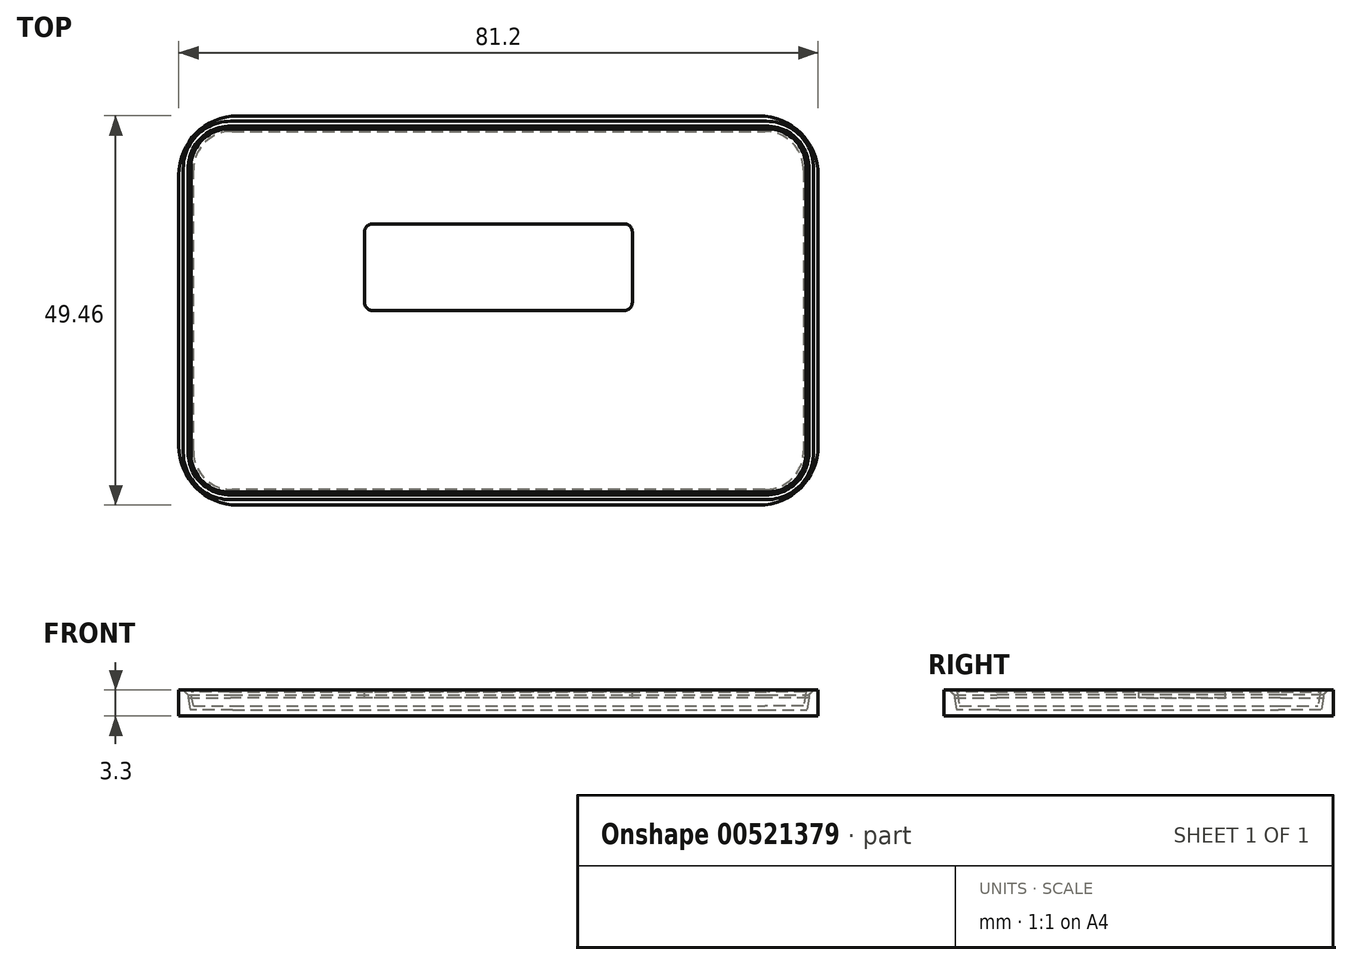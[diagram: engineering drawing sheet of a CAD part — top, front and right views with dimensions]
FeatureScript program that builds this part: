
annotation { "Feature Type Name" : "Feature", "Feature Type Description" : "" }
export const myFeature = defineFeature(function(context is Context, id is Id, definition is map)
    precondition{}
    {
        {
            var Q0;
            Q0=qCreatedBy(makeId("Top.planeOp"),FACE);
            var sketch = newSketch(context, id + "F0", { "sketchPlane" : qUnion([Q0])});
            skLineSegment(sketch, "E0.bottom", {"start": v(-38.75, 22.75) * mm, "end": v(38.75, 22.75) * mm});
            skLineSegment(sketch, "E0.top", {"start": v(-38.75, -22.75) * mm, "end": v(38.75, -22.75) * mm});
            skLineSegment(sketch, "E0.left", {"start": v(-38.75, 22.75) * mm, "end": v(-38.75, -22.75) * mm});
            skLineSegment(sketch, "E0.right", {"start": v(38.75, 22.75) * mm, "end": v(38.75, -22.75) * mm});
            skPoint(sketch, "E0.middle", {"position": v(0, 0) * mm});
            skSolve(sketch);
        }
        {
            var Q0;
            Q0 = qSketchRegion(id + "F0", true);
            extrude(context, id + "F1", {"entities" : qUnion([Q0]), "depth" : 1.8 * mm, "offsetDistance" : 25 * mm, "hasDraft" : true, "draftAngle" : 10 * degree});
        }
        {
            var Q0;
            Q0=makeQuery(id+"F1.opExtrude","SWEPT_EDGE",EDGE,{"disambiguationData":[OSD([sQuery(id+"F0.wireOp",EDGE,"E0.bottom"),sQuery(id+"F0.wireOp",EDGE,"E0.left")])]});
            var Q1;
            Q1=makeQuery(id+"F1.opExtrude","SWEPT_EDGE",EDGE,{"disambiguationData":[OSD([sQuery(id+"F0.wireOp",EDGE,"E0.top"),sQuery(id+"F0.wireOp",EDGE,"E0.left")])]});
            var Q2;
            Q2=makeQuery(id+"F1.opExtrude","SWEPT_EDGE",EDGE,{"disambiguationData":[OSD([sQuery(id+"F0.wireOp",EDGE,"E0.top"),sQuery(id+"F0.wireOp",EDGE,"E0.right")])]});
            var Q3;
            Q3=makeQuery(id+"F1.opExtrude","SWEPT_EDGE",EDGE,{"disambiguationData":[OSD([sQuery(id+"F0.wireOp",EDGE,"E0.bottom"),sQuery(id+"F0.wireOp",EDGE,"E0.right")])]});
            fillet(context, id + "F2", {"entities" : qUnion([Q0, Q1, Q2, Q3]), "radius" : 5 * mm, "tangentPropagation" : true, "allowEdgeOverflow" : false});
        }
        {
            var Q0;
            Q0=makeQuery(id+"F1.opExtrude","CAP_FACE",FACE,{"disambiguationData":[OSD([sQuery(id+"F0.wireOp",EDGE,"E0.bottom"),sQuery(id+"F0.wireOp",EDGE,"E0.top"),sQuery(id+"F0.wireOp",EDGE,"E0.left"),sQuery(id+"F0.wireOp",EDGE,"E0.right")])],"isStart":false});
            var sketch = newSketch(context, id + "F3", { "sketchPlane" : qUnion([Q0])});
            skLineSegment(sketch, "E1.bottom", {"start": v(16, 0) * mm, "end": v(-16, 0) * mm});
            skLineSegment(sketch, "E1.top", {"start": v(16, 11) * mm, "end": v(-16, 11) * mm});
            skLineSegment(sketch, "E1.left", {"start": v(17, 1) * mm, "end": v(17, 10) * mm});
            skLineSegment(sketch, "E1.right", {"start": v(-17, 1) * mm, "end": v(-17, 10) * mm});
            skPoint(sketch, "E1.middle", {"position": v(0, 5.5) * mm});
            skPoint(sketch, "E2.visualSharp", {"position": v(-17, 11) * mm});
            skArc(sketch, "E2.filletArc", {"start": v(-16, 11) * mm, "mid": v(-16.7, 10.7) * mm, "end": v(-17, 10) * mm});
            skPoint(sketch, "E3.visualSharp", {"position": v(17, 11) * mm});
            skArc(sketch, "E3.filletArc", {"start": v(17, 10) * mm, "mid": v(16.7, 10.7) * mm, "end": v(16, 11) * mm});
            skPoint(sketch, "E4.visualSharp", {"position": v(17, 0) * mm});
            skArc(sketch, "E4.filletArc", {"start": v(16, 0) * mm, "mid": v(16.7, 0.3) * mm, "end": v(17, 1) * mm});
            skPoint(sketch, "E5.visualSharp", {"position": v(-17, 0) * mm});
            skArc(sketch, "E5.filletArc", {"start": v(-17, 1) * mm, "mid": v(-16.7, 0.3) * mm, "end": v(-16, 0) * mm});
            skSolve(sketch);
        }
        {
            var Q0;
            Q0 = qSketchRegion(id + "F3", true);
            extrude(context, id + "F4", {"entities" : qUnion([Q0]), "operationType" : NewBodyOperationType.REMOVE, "oppositeDirection" : true, "depth" : 0.8 * mm, "offsetDistance" : 25 * mm});
        }
        {
            var Q0;
            Q0=qCreatedBy(makeId("Top.planeOp"),FACE);
            var sketch = newSketch(context, id + "F5", { "sketchPlane" : qUnion([Q0])});
            skLineSegment(sketch, "E6.0.0", {"start": v(-33.83, -22.75) * mm, "end": v(33.83, -22.75) * mm});
            skArc(sketch, "E6.0.1", {"start": v(-33.1, -22.23) * mm, "mid": v(-36.44, -20.94) * mm, "end": v(-38.07, -17.75) * mm});
            skLineSegment(sketch, "E6.0.2", {"start": v(-38.75, 17.83) * mm, "end": v(-38.75, -17.83) * mm});
            skArc(sketch, "E6.0.3", {"start": v(-38.1, 17.23) * mm, "mid": v(-36.86, 20.52) * mm, "end": v(-33.75, 22.18) * mm});
            skLineSegment(sketch, "E6.0.4", {"start": v(-33.83, 22.75) * mm, "end": v(33.83, 22.75) * mm});
            skArc(sketch, "E6.0.5", {"start": v(33.1, 22.23) * mm, "mid": v(36.44, 20.94) * mm, "end": v(38.07, 17.75) * mm});
            skLineSegment(sketch, "E6.0.6", {"start": v(38.75, 17.83) * mm, "end": v(38.75, -17.83) * mm});
            skArc(sketch, "E6.0.7", {"start": v(38.1, -17.23) * mm, "mid": v(36.64, -20.76) * mm, "end": v(33.1, -22.23) * mm});
            skArc(sketch, "E7.0", {"start": v(40.6, -17.23) * mm, "mid": v(38.4, -22.53) * mm, "end": v(33.1, -24.73) * mm});
            skLineSegment(sketch, "E7.1", {"start": v(40.6, 17.23) * mm, "end": v(40.6, -17.23) * mm});
            skLineSegment(sketch, "E7.2", {"start": v(33.1, -24.73) * mm, "end": v(-33.1, -24.73) * mm});
            skArc(sketch, "E7.3", {"start": v(33.1, 24.73) * mm, "mid": v(38.4, 22.53) * mm, "end": v(40.6, 17.23) * mm});
            skArc(sketch, "E7.4", {"start": v(-33.1, -24.73) * mm, "mid": v(-38.4, -22.53) * mm, "end": v(-40.6, -17.23) * mm});
            skLineSegment(sketch, "E7.5", {"start": v(-40.6, -17.23) * mm, "end": v(-40.6, 17.23) * mm});
            skArc(sketch, "E7.6", {"start": v(-40.6, 17.23) * mm, "mid": v(-38.4, 22.53) * mm, "end": v(-33.1, 24.73) * mm});
            skLineSegment(sketch, "E7.7", {"start": v(-33.1, 24.73) * mm, "end": v(33.1, 24.73) * mm});
            skSolve(sketch);
        }
        {
            var Q0;
            Q0 = qSketchRegion(id + "F5", true);
            var Q1;
            Q1=makeQuery(id+"F5.imprint","IMPRINT",FACE,{"disambiguationData":[TD([[makeQuery(id+"F5.imprint","IMPRINT",EDGE,{"derivedFrom":sQuery(id+"F5.wireOp",EDGE,"E6.0.0")}),-1.0]])]});
            var Q2;
            Q2=makeQuery(id+"F4.boolean.opBoolean","COPY",FACE,{"derivedFrom":makeQuery(id+"F4.opExtrude","CAP_FACE",FACE,{"disambiguationData":[OSD([sQuery(id+"F3.wireOp",EDGE,"E1.bottom"),sQuery(id+"F3.wireOp",EDGE,"E1.top"),sQuery(id+"F3.wireOp",EDGE,"E1.left"),sQuery(id+"F3.wireOp",EDGE,"E1.right"),sQuery(id+"F3.wireOp",EDGE,"E2.filletArc"),sQuery(id+"F3.wireOp",EDGE,"E3.filletArc"),sQuery(id+"F3.wireOp",EDGE,"E4.filletArc"),sQuery(id+"F3.wireOp",EDGE,"E5.filletArc")])],"isStart":false})});
            extrude(context, id + "F6", {"entities" : qUnion([Q0, Q1]), "endBound" : BoundingType.UP_TO_SURFACE, "depth" : 2 * mm, "endBoundEntityFace" : qUnion([Q2]), "offsetDistance" : 25 * mm, "hasSecondDirection" : true, "secondDirectionOppositeDirection" : true, "secondDirectionDepth" : 1.3 * mm});
        }
        {
            var Q0;
            Q0=makeQuery(id+"F1.opExtrude","SWEPT_BODY",BODY,{"disambiguationData":[OSD([sQuery(id+"F0.wireOp",EDGE,"E0.bottom"),sQuery(id+"F0.wireOp",EDGE,"E0.top"),sQuery(id+"F0.wireOp",EDGE,"E0.left"),sQuery(id+"F0.wireOp",EDGE,"E0.right")])]});
            var Q1;
            Q1=makeQuery(id+"F6.opExtrude","SWEPT_BODY",BODY,{"disambiguationData":[OSD([sQuery(id+"F5.wireOp",EDGE,"E7.0"),sQuery(id+"F5.wireOp",EDGE,"E7.1"),sQuery(id+"F5.wireOp",EDGE,"E7.2"),sQuery(id+"F5.wireOp",EDGE,"E7.3"),sQuery(id+"F5.wireOp",EDGE,"E7.4"),sQuery(id+"F5.wireOp",EDGE,"E7.5"),sQuery(id+"F5.wireOp",EDGE,"E7.6"),sQuery(id+"F5.wireOp",EDGE,"E7.7")])]});
            var Q2;
            Q2=makeQuery(id+"F1.opExtrude","SWEPT_FACE",FACE,{"disambiguationData":[OSD([sQuery(id+"F0.wireOp",EDGE,"E0.top")])]});
            var Q3;
            Q3=makeQuery(id+"F2.opFillet","BLEND_FACE",FACE,{"disambiguationData":[OSD([sQuery(id+"F0.wireOp",EDGE,"E0.top"),sQuery(id+"F0.wireOp",EDGE,"E0.right")])]});
            var Q4;
            Q4=makeQuery(id+"F1.opExtrude","SWEPT_FACE",FACE,{"disambiguationData":[OSD([sQuery(id+"F0.wireOp",EDGE,"E0.right")])]});
            booleanBodies(context, id + "F7", {"operationType" : BooleanOperationType.SUBTRACTION, "tools" : qUnion([Q0]), "targets" : qUnion([Q1]), "offset" : true, "offsetAll" : true, "entitiesToOffset" : qUnion([Q2, Q3, Q4]), "offsetDistance" : .5 * mm, "keepTools" : true});
        }
        {
            var Q0;
            Q0=makeQuery(id+"F6.opExtrude","CAP_FACE",FACE,{"disambiguationData":[OSD([sQuery(id+"F5.wireOp",EDGE,"E7.0"),sQuery(id+"F5.wireOp",EDGE,"E7.1"),sQuery(id+"F5.wireOp",EDGE,"E7.2"),sQuery(id+"F5.wireOp",EDGE,"E7.3"),sQuery(id+"F5.wireOp",EDGE,"E7.4"),sQuery(id+"F5.wireOp",EDGE,"E7.5"),sQuery(id+"F5.wireOp",EDGE,"E7.6"),sQuery(id+"F5.wireOp",EDGE,"E7.7")])],"isStart":false});
            extrude(context, id + "F8", {"entities" : qUnion([Q0]), "operationType" : NewBodyOperationType.ADD, "depth" : 1 * mm, "offsetDistance" : 25 * mm});
        }
        {
            var Q0;
            Q0=makeQuery(id+"F8.opExtrude","CAP_EDGE",EDGE,{"disambiguationData":[OSD([sQuery(id+"F0.wireOp",EDGE,"E0.right"),sQuery(id+"F3.wireOp",EDGE,"E1.bottom"),sQuery(id+"F3.wireOp",EDGE,"E1.top"),sQuery(id+"F3.wireOp",EDGE,"E1.left"),sQuery(id+"F3.wireOp",EDGE,"E1.right"),sQuery(id+"F3.wireOp",EDGE,"E2.filletArc"),sQuery(id+"F3.wireOp",EDGE,"E3.filletArc"),sQuery(id+"F3.wireOp",EDGE,"E4.filletArc"),sQuery(id+"F3.wireOp",EDGE,"E5.filletArc")])],"isStart":false});
            chamfer(context, id + "F9", {"entities" : qUnion([Q0]), "width" : .6 * mm, "tangentPropagation" : true});
        }
    });
